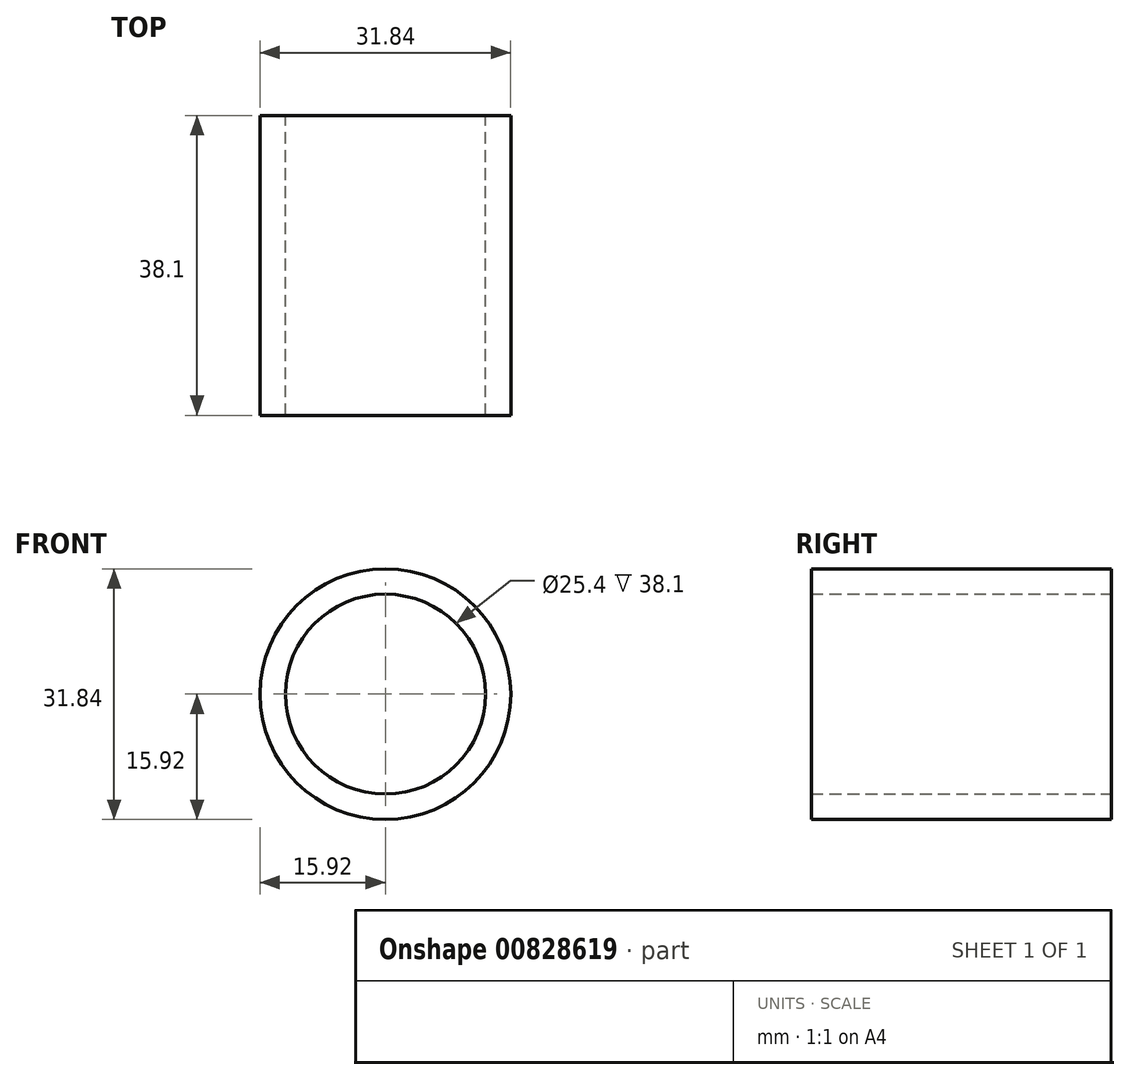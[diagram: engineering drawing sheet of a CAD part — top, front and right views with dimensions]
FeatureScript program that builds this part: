
annotation { "Feature Type Name" : "Feature", "Feature Type Description" : "" }
export const myFeature = defineFeature(function(context is Context, id is Id, definition is map)
    precondition{}
    {
        {
            var Q0;
            Q0=qCreatedBy(makeId("Front.planeOp"),FACE);
            var sketch = newSketch(context, id + "F0", { "sketchPlane" : qUnion([Q0])});
            skCircle(sketch, "E0", {"center": v(0, 0) * mm, "radius": 12.7 * mm});
            skCircle(sketch, "E1", {"center": v(0, 0) * mm, "radius": 15.92 * mm});
            skSolve(sketch);
        }
        {
            var Q0;
            Q0=makeQuery(id+"F0.imprint","IMPRINT",FACE,{"disambiguationData":[TD([[makeQuery(id+"F0.imprint","IMPRINT",EDGE,{"derivedFrom":sQuery(id+"F0.wireOp",EDGE,"E0")}),-1.0]])]});
            extrude(context, id + "F1", {"entities" : qUnion([Q0]), "depth" : 38.1 * mm, "offsetDistance" : 25.4 * mm});
        }
    });
